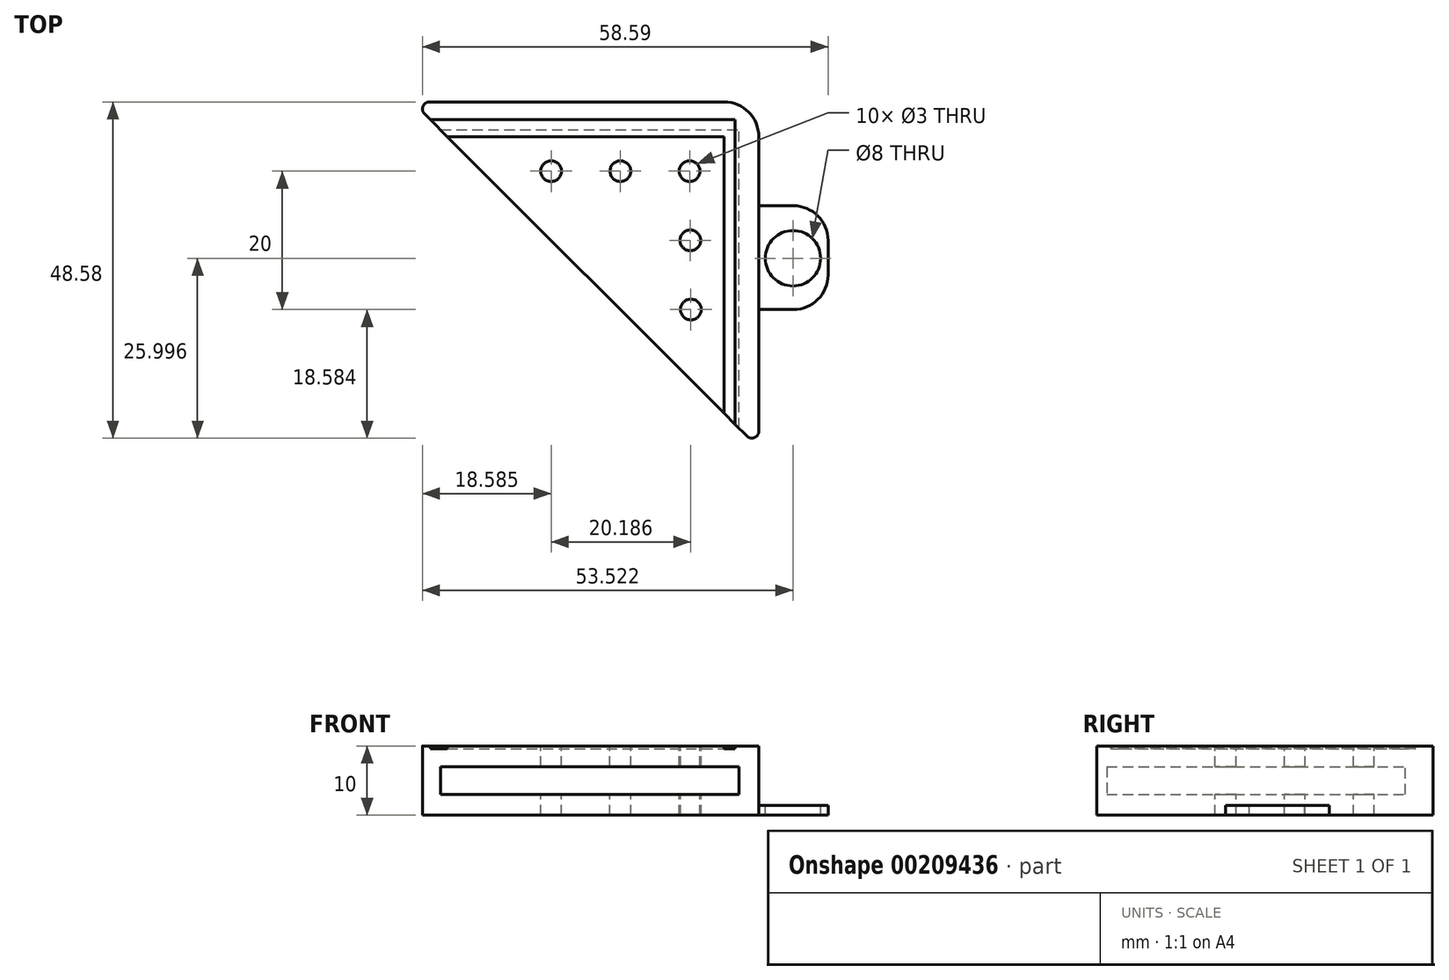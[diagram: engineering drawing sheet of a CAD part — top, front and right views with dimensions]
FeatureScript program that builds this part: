
annotation { "Feature Type Name" : "Feature", "Feature Type Description" : "" }
export const myFeature = defineFeature(function(context is Context, id is Id, definition is map)
    precondition{}
    {
        {
            var Q0;
            Q0=qCreatedBy(makeId("Top.planeOp"),FACE);
            var sketch = newSketch(context, id + "F0", { "sketchPlane" : qUnion([Q0])});
            skLineSegment(sketch, "E0", {"start": v(-24, 35.32) * mm, "end": v(26, 35.32) * mm});
            skLineSegment(sketch, "E1", {"start": v(26, 35.32) * mm, "end": v(26, -14.68) * mm});
            skLineSegment(sketch, "E2", {"start": v(26, -14.68) * mm, "end": v(-24, 35.32) * mm});
            skSolve(sketch);
        }
        {
            var Q0;
            Q0=makeQuery(id+"F0.imprint","IMPRINT",FACE,{"disambiguationData":[TD([[makeQuery(id+"F0.imprint","IMPRINT",EDGE,{"derivedFrom":sQuery(id+"F0.wireOp",EDGE,"E0")}),-1.0]])]});
            extrude(context, id + "F1", {"entities" : qUnion([Q0]), "depth" : 10 * mm});
        }
        {
            var Q0;
            Q0=makeQuery(id+"F1.opExtrude","SWEPT_FACE",FACE,{"disambiguationData":[OSD([sQuery(id+"F0.wireOp",EDGE,"E1")])]});
            var sketch = newSketch(context, id + "F2", { "sketchPlane" : qUnion([Q0])});
            skLineSegment(sketch, "E3.bottom", {"start": v(31.3, 7) * mm, "end": v(-14.68, 7) * mm});
            skLineSegment(sketch, "E3.top", {"start": v(31.3, 3) * mm, "end": v(-14.68, 3) * mm});
            skLineSegment(sketch, "E3.left", {"start": v(31.3, 7) * mm, "end": v(31.3, 3) * mm});
            skLineSegment(sketch, "E3.right", {"start": v(-14.68, 7) * mm, "end": v(-14.68, 3) * mm});
            skSolve(sketch);
        }
        {
            var Q0;
            Q0=qSketchRegion(id+"F2",true);
            extrude(context, id + "F3", {"entities" : qUnion([Q0]), "operationType" : NewBodyOperationType.REMOVE, "oppositeDirection" : true, "depth" : 63.9 * mm});
        }
        {
            var Q0;
            Q0=makeQuery(id+"F3.boolean.opBoolean","COPY",FACE,{"derivedFrom":makeQuery(id+"F3.opExtrude","SWEPT_FACE",FACE,{"disambiguationData":[OSD([sQuery(id+"F2.wireOp",EDGE,"E3.left")])]})});
            var sketch = newSketch(context, id + "F4", { "sketchPlane" : qUnion([Q0])});
            skLineSegment(sketch, "E4.bottom", {"start": v(23.15, 3) * mm, "end": v(26, 3) * mm});
            skLineSegment(sketch, "E4.top", {"start": v(23.15, 7) * mm, "end": v(26, 7) * mm});
            skLineSegment(sketch, "E4.left", {"start": v(23.15, 3) * mm, "end": v(23.15, 7) * mm});
            skLineSegment(sketch, "E4.right", {"start": v(26, 3) * mm, "end": v(26, 7) * mm});
            skSolve(sketch);
        }
        {
            var Q0;
            Q0=qSketchRegion(id+"F4",true);
            extrude(context, id + "F5", {"entities" : qUnion([Q0]), "operationType" : NewBodyOperationType.ADD, "depth" : 45.56 * mm});
        }
        {
            var Q0;
            Q0=makeQuery(id+"F5.opExtrude","SWEPT_FACE",FACE,{"disambiguationData":[OSD([sQuery(id+"F4.wireOp",EDGE,"E4.top")])]});
            var sketch = newSketch(context, id + "F6", { "sketchPlane" : qUnion([Q0])});
            skLineSegment(sketch, "E5", {"start": v(26, -14.68) * mm, "end": v(23.15, -14.26) * mm});
            skLineSegment(sketch, "E6", {"start": v(23.15, -14.26) * mm, "end": v(23.15, -11.83) * mm});
            skLineSegment(sketch, "E7", {"start": v(23.15, -11.83) * mm, "end": v(26, -14.68) * mm});
            skSolve(sketch);
        }
        {
            var Q0;
            Q0=makeQuery(id+"F6.imprint","IMPRINT",FACE,{"disambiguationData":[TD([[makeQuery(id+"F6.imprint","IMPRINT",EDGE,{"derivedFrom":sQuery(id+"F6.wireOp",EDGE,"E5")}),-1.0]])]});
            var sketch = newSketch(context, id + "F7", { "sketchPlane" : qUnion([Q0])});
            skLineSegment(sketch, "E8", {"start": v(23.15, -14.7) * mm, "end": v(26.02, -14.7) * mm});
            skLineSegment(sketch, "E9", {"start": v(26.02, -14.7) * mm, "end": v(23.14, -11.82) * mm});
            skLineSegment(sketch, "E10", {"start": v(23.14, -11.82) * mm, "end": v(23.15, -14.7) * mm});
            skSolve(sketch);
        }
        {
            var Q0;
            Q0=qSketchRegion(id+"F7",true);
            extrude(context, id + "F8", {"entities" : qUnion([Q0]), "operationType" : NewBodyOperationType.REMOVE, "oppositeDirection" : true, "depth" : 25 * mm});
        }
        {
            var Q0;
            {var subQ0=sQuery(id+"F0.wireOp",EDGE,"E2");var subQ1=sQuery(id+"F0.wireOp",EDGE,"E1");Q0=makeQuery(id+"F3.boolean.opBoolean","SPLIT",EDGE,{"disambiguationData":[TD([makeQuery(id+"F3.opExtrude","SWEPT_FACE",FACE,{"disambiguationData":[OSD([sQuery(id+"F2.wireOp",EDGE,"E3.bottom")])]})])],"derivedFrom":makeQuery(id+"F1.opExtrude","SWEPT_EDGE",EDGE,{"disambiguationData":[OSD([subQ1,subQ0])]})});}
            fillet(context, id + "F9", {"entities" : qUnion([Q0]), "radius" : 1 * mm, "tangentPropagation" : true, "allowEdgeOverflow" : false});
        }
        {
            var Q0;
            Q0=makeQuery(id+"F1.opExtrude","SWEPT_EDGE",EDGE,{"disambiguationData":[OSD([sQuery(id+"F0.wireOp",EDGE,"E0"),sQuery(id+"F0.wireOp",EDGE,"E2")])]});
            fillet(context, id + "F10", {"entities" : qUnion([Q0]), "radius" : 1 * mm, "tangentPropagation" : true, "allowEdgeOverflow" : false});
        }
        {
            var Q0;
            Q0=makeQuery(id+"F1.opExtrude","CAP_FACE",FACE,{"disambiguationData":[OSD([sQuery(id+"F0.wireOp",EDGE,"E0"),sQuery(id+"F0.wireOp",EDGE,"E1"),sQuery(id+"F0.wireOp",EDGE,"E2")])],"isStart":false});
            var sketch = newSketch(context, id + "F11", { "sketchPlane" : qUnion([Q0])});
            skCircle(sketch, "E11", {"center": v(-4, 25.32) * mm, "radius": 1.5 * mm});
            skCircle(sketch, "E12", {"center": v(6, 25.32) * mm, "radius": 1.5 * mm});
            skCircle(sketch, "E13", {"center": v(16, 25.32) * mm, "radius": 1.5 * mm});
            skCircle(sketch, "E14", {"center": v(16.1, 15.32) * mm, "radius": 1.5 * mm});
            skCircle(sketch, "E15", {"center": v(16.18, 5.32) * mm, "radius": 1.5 * mm});
            skSolve(sketch);
        }
        {
            var Q0;
            Q0=makeQuery(id+"F11.imprint","IMPRINT",FACE,{"disambiguationData":[TD([[makeQuery(id+"F11.imprint","IMPRINT",EDGE,{"derivedFrom":sQuery(id+"F11.wireOp",EDGE,"E12")}),1.0]])]});
            var Q1;
            Q1=makeQuery(id+"F11.imprint","IMPRINT",FACE,{"disambiguationData":[TD([[makeQuery(id+"F11.imprint","IMPRINT",EDGE,{"derivedFrom":sQuery(id+"F11.wireOp",EDGE,"E11")}),1.0]])]});
            var Q2;
            Q2=makeQuery(id+"F11.imprint","IMPRINT",FACE,{"disambiguationData":[TD([[makeQuery(id+"F11.imprint","IMPRINT",EDGE,{"derivedFrom":sQuery(id+"F11.wireOp",EDGE,"E13")}),1.0]])]});
            var Q3;
            Q3=makeQuery(id+"F11.imprint","IMPRINT",FACE,{"disambiguationData":[TD([[makeQuery(id+"F11.imprint","IMPRINT",EDGE,{"derivedFrom":sQuery(id+"F11.wireOp",EDGE,"E14")}),1.0]])]});
            var Q4;
            Q4=makeQuery(id+"F11.imprint","IMPRINT",FACE,{"disambiguationData":[TD([[makeQuery(id+"F11.imprint","IMPRINT",EDGE,{"derivedFrom":sQuery(id+"F11.wireOp",EDGE,"E15")}),1.0]])]});
            extrude(context, id + "F12", {"entities" : qUnion([Q0, Q1, Q2, Q3, Q4]), "operationType" : NewBodyOperationType.REMOVE, "oppositeDirection" : true, "depth" : 25 * mm});
        }
        {
            var Q0;
            Q0=makeQuery(id+"F1.opExtrude","SWEPT_EDGE",EDGE,{"disambiguationData":[OSD([sQuery(id+"F0.wireOp",EDGE,"E0"),sQuery(id+"F0.wireOp",EDGE,"E1")])]});
            fillet(context, id + "F13", {"entities" : qUnion([Q0]), "radius" : 5 * mm, "tangentPropagation" : true, "allowEdgeOverflow" : false});
        }
        {
            var Q0;
            Q0=makeQuery(id+"F1.opExtrude","CAP_FACE",FACE,{"disambiguationData":[OSD([sQuery(id+"F0.wireOp",EDGE,"E0"),sQuery(id+"F0.wireOp",EDGE,"E1"),sQuery(id+"F0.wireOp",EDGE,"E2")])],"isStart":false});
            var sketch = newSketch(context, id + "F14", { "sketchPlane" : qUnion([Q0])});
            skLineSegment(sketch, "E16", {"start": v(-21.44, 32.76) * mm, "end": v(22.59, 32.76) * mm});
            skLineSegment(sketch, "E17", {"start": v(22.59, 32.76) * mm, "end": v(22.59, -11.27) * mm});
            skLineSegment(sketch, "E18", {"start": v(22.59, -11.27) * mm, "end": v(21, -9.68) * mm});
            skLineSegment(sketch, "E19", {"start": v(21, -9.68) * mm, "end": v(21, 30.32) * mm});
            skLineSegment(sketch, "E20", {"start": v(21, 30.32) * mm, "end": v(-19, 30.32) * mm});
            skLineSegment(sketch, "E21", {"start": v(-19, 30.32) * mm, "end": v(-21.44, 32.76) * mm});
            skSolve(sketch);
        }
        {
            var Q0;
            Q0=qSketchRegion(id+"F14",true);
            extrude(context, id + "F15", {"entities" : qUnion([Q0]), "operationType" : NewBodyOperationType.REMOVE, "oppositeDirection" : true, "depth" : 0.4 * mm});
        }
        {
            var Q0;
            Q0=makeQuery(id+"F5.boolean.opBoolean","MERGE",FACE,{"derivedFrom":[makeQuery(id+"F1.opExtrude","SWEPT_FACE",FACE,{"disambiguationData":[OSD([sQuery(id+"F0.wireOp",EDGE,"E1")])]}),makeQuery(id+"F5.opExtrude","SWEPT_FACE",FACE,{"disambiguationData":[OSD([sQuery(id+"F4.wireOp",EDGE,"E4.right")])]})]});
            var sketch = newSketch(context, id + "F16", { "sketchPlane" : qUnion([Q0])});
            skLineSegment(sketch, "E22.bottom", {"start": v(5.32, 0) * mm, "end": v(20.32, 0) * mm});
            skLineSegment(sketch, "E22.top", {"start": v(5.32, 1.4) * mm, "end": v(20.32, 1.4) * mm});
            skLineSegment(sketch, "E22.left", {"start": v(5.32, 0) * mm, "end": v(5.32, 1.4) * mm});
            skLineSegment(sketch, "E22.right", {"start": v(20.32, 0) * mm, "end": v(20.32, 1.4) * mm});
            skSolve(sketch);
        }
        {
            var Q0;
            Q0 = qSketchRegion(id + "F16", true);
            extrude(context, id + "F17", {"entities" : qUnion([Q0]), "operationType" : NewBodyOperationType.ADD, "depth" : 10 * mm});
        }
        {
            var Q0;
            Q0=makeQuery(id+"F17.opExtrude","SWEPT_FACE",FACE,{"disambiguationData":[OSD([sQuery(id+"F16.wireOp",EDGE,"E22.top")])]});
            var sketch = newSketch(context, id + "F18", { "sketchPlane" : qUnion([Q0])});
            skCircle(sketch, "E23", {"center": v(30.93, 12.74) * mm, "radius": 4 * mm});
            skSolve(sketch);
        }
        {
            var Q0;
            Q0=makeQuery(id+"F17.opExtrude","CAP_EDGE",EDGE,{"disambiguationData":[OSD([sQuery(id+"F16.wireOp",EDGE,"E22.right")])],"isStart":false});
            var Q1;
            Q1=makeQuery(id+"F17.opExtrude","CAP_EDGE",EDGE,{"disambiguationData":[OSD([sQuery(id+"F16.wireOp",EDGE,"E22.left")])],"isStart":false});
            fillet(context, id + "F19", {"entities" : qUnion([Q0, Q1]), "radius" : 5 * mm, "tangentPropagation" : true, "allowEdgeOverflow" : false});
        }
        {
            var Q0;
            Q0=makeQuery(id+"F18.imprint","IMPRINT",FACE,{"disambiguationData":[TD([[makeQuery(id+"F18.imprint","IMPRINT",EDGE,{"derivedFrom":sQuery(id+"F18.wireOp",EDGE,"E23")}),1.0]])]});
            extrude(context, id + "F20", {"entities" : qUnion([Q0]), "operationType" : NewBodyOperationType.REMOVE, "oppositeDirection" : true, "depth" : 25 * mm});
        }
    });
